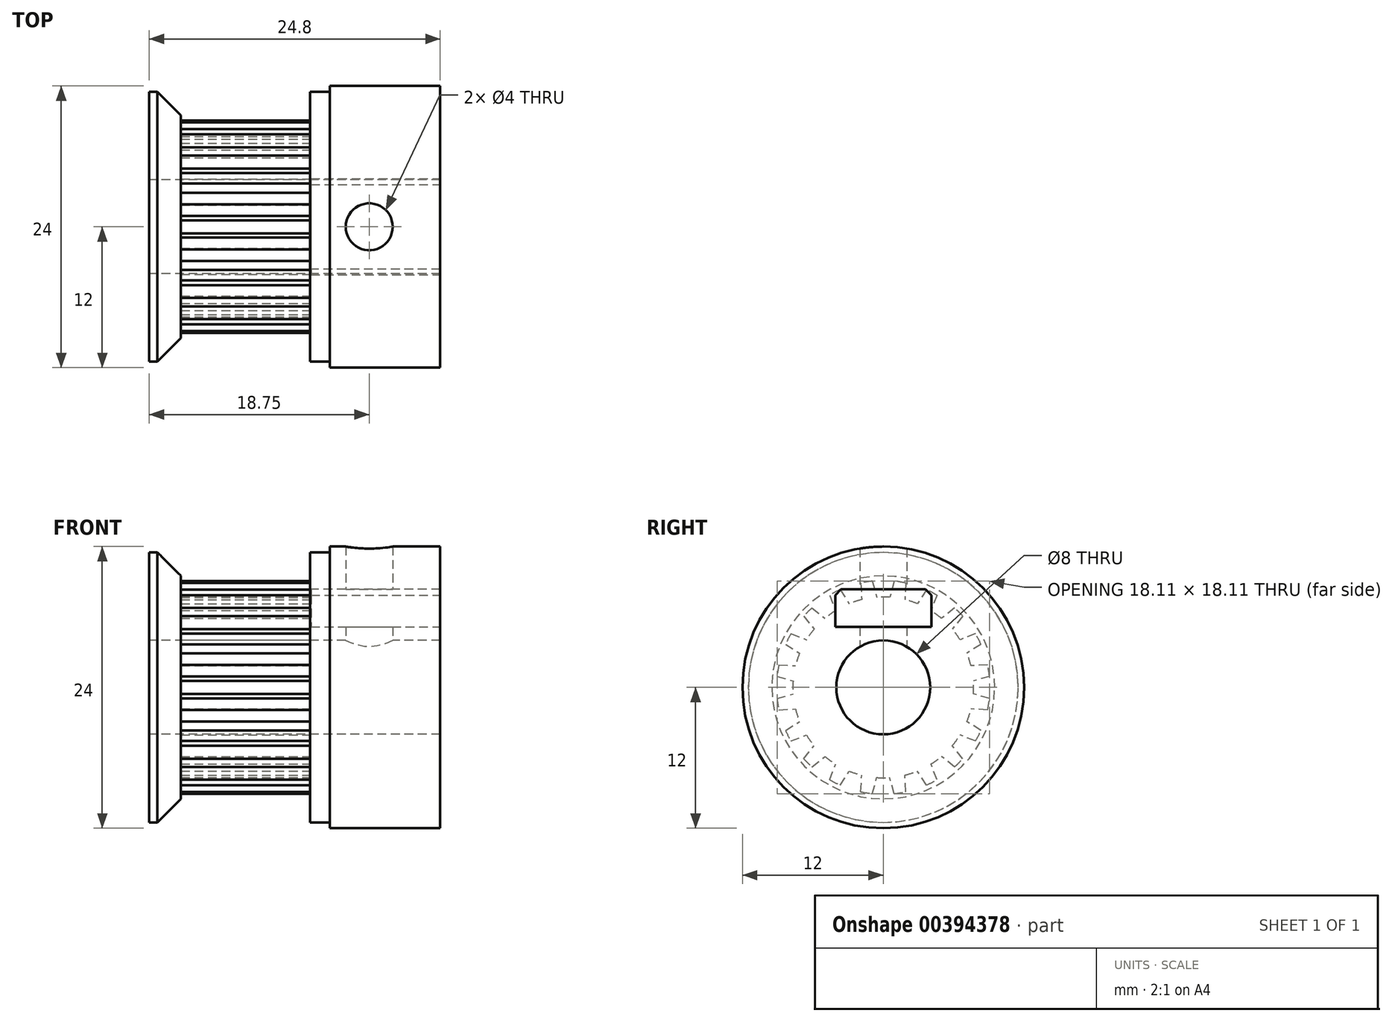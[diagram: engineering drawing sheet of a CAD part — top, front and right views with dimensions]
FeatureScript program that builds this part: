
annotation { "Feature Type Name" : "Feature", "Feature Type Description" : "" }
export const myFeature = defineFeature(function(context is Context, id is Id, definition is map)
    precondition{}
    {
        {
            var Q0;
            Q0=qCreatedBy(makeId("Top.planeOp"),FACE);
            var sketch = newSketch(context, id + "F0", { "sketchPlane" : qUnion([Q0])});
            skLineSegment(sketch, "E0", {"start": v(0, 0) * mm, "end": v(0, 231.14) * mm, "construction": true});
            skLineSegment(sketch, "E1", {"start": v(-182.88, 231.14) * mm, "end": v(182.88, 231.14) * mm});
            skPoint(sketch, "E2", {"position": v(0, 231.14) * mm});
            skLineSegment(sketch, "E3", {"start": v(-182.88, 231.14) * mm, "end": v(-182.88, 0) * mm});
            skLineSegment(sketch, "E4", {"start": v(-182.88, 101.6) * mm, "end": v(421.64, 101.6) * mm});
            skLineSegment(sketch, "E5", {"start": v(182.88, 304.8) * mm, "end": v(421.64, 304.8) * mm});
            skLineSegment(sketch, "E6", {"start": v(182.88, 304.8) * mm, "end": v(182.88, 231.14) * mm});
            skLineSegment(sketch, "E7", {"start": v(421.64, 304.8) * mm, "end": v(421.64, 101.6) * mm});
            skLineSegment(sketch, "E8", {"start": v(0, 0) * mm, "end": v(573.1, 0) * mm});
            skSolve(sketch);
        }
        {
            var Q0;
            {var subQ2=sQuery(id+"F0.wireOp",EDGE,"E1");Q0=makeQuery(id+"F0.imprint","IMPRINT",FACE,{"disambiguationData":[TD([[makeQuery(id+"F0.imprint","IMPRINT",EDGE,{"derivedFrom":subQ2}),-1.0]])]});}
            var Q1;
            Q1=sQuery(id+"F0.wireOp",EDGE,"E8");
            revolve(context, id + "F1", {"entities" : qUnion([Q0]), "axis" : qUnion([Q1]), "revolveType" : RevolveType.FULL});
        }
        {
            var Q0;
            Q0=qCreatedBy(makeId("Right.planeOp"),FACE);
            var sketch = newSketch(context, id + "F2", { "sketchPlane" : qUnion([Q0])});
            skLineSegment(sketch, "E9", {"start": v(0, 0) * mm, "end": v(0, 231.14) * mm, "construction": true});
            skLineSegment(sketch, "E10", {"start": v(23.56, 229.94) * mm, "end": v(14.22, 195.06) * mm});
            skCircle(sketch, "E11", {"center": v(0, 0) * mm, "radius": 231.14 * mm});
            skCircle(sketch, "E12", {"center": v(0, 0) * mm, "radius": 195.58 * mm});
            skLineSegment(sketch, "E13.MirrorCS", {"start": v(-23.56, 229.94) * mm, "end": v(-14.22, 195.06) * mm});
            skLineSegment(sketch, "E14.1.0", {"start": v(0, 0) * mm, "end": v(-71.43, 219.83) * mm, "construction": true});
            skLineSegment(sketch, "E14.1.1", {"start": v(-48.65, 225.96) * mm, "end": v(-46.76, 189.9) * mm});
            skLineSegment(sketch, "E14.1.2", {"start": v(-93.46, 211.4) * mm, "end": v(-73.8, 181.12) * mm});
            skLineSegment(sketch, "E14.2.0", {"start": v(0, 0) * mm, "end": v(-135.86, 187) * mm, "construction": true});
            skLineSegment(sketch, "E14.2.1", {"start": v(-116.1, 199.87) * mm, "end": v(-103.15, 166.16) * mm});
            skLineSegment(sketch, "E14.2.2", {"start": v(-154.21, 172.17) * mm, "end": v(-126.16, 149.45) * mm});
            skLineSegment(sketch, "E14.3.0", {"start": v(0, 0) * mm, "end": v(-187, 135.86) * mm, "construction": true});
            skLineSegment(sketch, "E14.3.1", {"start": v(-172.17, 154.21) * mm, "end": v(-149.45, 126.16) * mm});
            skLineSegment(sketch, "E14.3.2", {"start": v(-199.87, 116.1) * mm, "end": v(-166.16, 103.15) * mm});
            skLineSegment(sketch, "E14.4.0", {"start": v(0, 0) * mm, "end": v(-219.83, 71.43) * mm, "construction": true});
            skLineSegment(sketch, "E14.4.1", {"start": v(-211.4, 93.46) * mm, "end": v(-181.12, 73.8) * mm});
            skLineSegment(sketch, "E14.4.2", {"start": v(-225.96, 48.65) * mm, "end": v(-189.9, 46.76) * mm});
            skLineSegment(sketch, "E14.5.0", {"start": v(0, 0) * mm, "end": v(-231.14, 0) * mm, "construction": true});
            skLineSegment(sketch, "E14.5.1", {"start": v(-229.94, 23.56) * mm, "end": v(-195.06, 14.22) * mm});
            skLineSegment(sketch, "E14.5.2", {"start": v(-229.94, -23.56) * mm, "end": v(-195.06, -14.22) * mm});
            skLineSegment(sketch, "E14.6.0", {"start": v(0, 0) * mm, "end": v(-219.83, -71.43) * mm, "construction": true});
            skLineSegment(sketch, "E14.6.1", {"start": v(-225.96, -48.65) * mm, "end": v(-189.9, -46.76) * mm});
            skLineSegment(sketch, "E14.6.2", {"start": v(-211.4, -93.46) * mm, "end": v(-181.12, -73.8) * mm});
            skLineSegment(sketch, "E14.7.0", {"start": v(0, 0) * mm, "end": v(-187, -135.86) * mm, "construction": true});
            skLineSegment(sketch, "E14.7.1", {"start": v(-199.87, -116.1) * mm, "end": v(-166.16, -103.15) * mm});
            skLineSegment(sketch, "E14.7.2", {"start": v(-172.17, -154.21) * mm, "end": v(-149.45, -126.16) * mm});
            skLineSegment(sketch, "E14.8.0", {"start": v(0, 0) * mm, "end": v(-135.86, -187) * mm, "construction": true});
            skLineSegment(sketch, "E14.8.1", {"start": v(-154.21, -172.17) * mm, "end": v(-126.16, -149.45) * mm});
            skLineSegment(sketch, "E14.8.2", {"start": v(-116.1, -199.87) * mm, "end": v(-103.15, -166.16) * mm});
            skLineSegment(sketch, "E14.9.0", {"start": v(0, 0) * mm, "end": v(-71.43, -219.83) * mm, "construction": true});
            skLineSegment(sketch, "E14.9.1", {"start": v(-93.46, -211.4) * mm, "end": v(-73.8, -181.12) * mm});
            skLineSegment(sketch, "E14.9.2", {"start": v(-48.65, -225.96) * mm, "end": v(-46.76, -189.9) * mm});
            skLineSegment(sketch, "E14.10.0", {"start": v(0, 0) * mm, "end": v(0, -231.14) * mm, "construction": true});
            skLineSegment(sketch, "E14.10.1", {"start": v(-23.56, -229.94) * mm, "end": v(-14.22, -195.06) * mm});
            skLineSegment(sketch, "E14.10.2", {"start": v(23.56, -229.94) * mm, "end": v(14.22, -195.06) * mm});
            skLineSegment(sketch, "E14.11.0", {"start": v(0, 0) * mm, "end": v(71.43, -219.83) * mm, "construction": true});
            skLineSegment(sketch, "E14.11.1", {"start": v(48.65, -225.96) * mm, "end": v(46.76, -189.9) * mm});
            skLineSegment(sketch, "E14.11.2", {"start": v(93.46, -211.4) * mm, "end": v(73.8, -181.12) * mm});
            skLineSegment(sketch, "E14.12.0", {"start": v(0, 0) * mm, "end": v(135.86, -187) * mm, "construction": true});
            skLineSegment(sketch, "E14.12.1", {"start": v(116.1, -199.87) * mm, "end": v(103.15, -166.16) * mm});
            skLineSegment(sketch, "E14.12.2", {"start": v(154.21, -172.17) * mm, "end": v(126.16, -149.45) * mm});
            skLineSegment(sketch, "E14.13.0", {"start": v(0, 0) * mm, "end": v(187, -135.86) * mm, "construction": true});
            skLineSegment(sketch, "E14.13.1", {"start": v(172.17, -154.21) * mm, "end": v(149.45, -126.16) * mm});
            skLineSegment(sketch, "E14.13.2", {"start": v(199.87, -116.1) * mm, "end": v(166.16, -103.15) * mm});
            skLineSegment(sketch, "E14.14.0", {"start": v(0, 0) * mm, "end": v(219.83, -71.43) * mm, "construction": true});
            skLineSegment(sketch, "E14.14.1", {"start": v(211.4, -93.46) * mm, "end": v(181.12, -73.8) * mm});
            skLineSegment(sketch, "E14.14.2", {"start": v(225.96, -48.65) * mm, "end": v(189.9, -46.76) * mm});
            skLineSegment(sketch, "E14.15.0", {"start": v(0, 0) * mm, "end": v(231.14, 0) * mm, "construction": true});
            skLineSegment(sketch, "E14.15.1", {"start": v(229.94, -23.56) * mm, "end": v(195.06, -14.22) * mm});
            skLineSegment(sketch, "E14.15.2", {"start": v(229.94, 23.56) * mm, "end": v(195.06, 14.22) * mm});
            skLineSegment(sketch, "E14.16.0", {"start": v(0, 0) * mm, "end": v(219.83, 71.43) * mm, "construction": true});
            skLineSegment(sketch, "E14.16.1", {"start": v(225.96, 48.65) * mm, "end": v(189.9, 46.76) * mm});
            skLineSegment(sketch, "E14.16.2", {"start": v(211.4, 93.46) * mm, "end": v(181.12, 73.8) * mm});
            skLineSegment(sketch, "E14.17.0", {"start": v(0, 0) * mm, "end": v(187, 135.86) * mm, "construction": true});
            skLineSegment(sketch, "E14.17.1", {"start": v(199.87, 116.1) * mm, "end": v(166.16, 103.15) * mm});
            skLineSegment(sketch, "E14.17.2", {"start": v(172.17, 154.21) * mm, "end": v(149.45, 126.16) * mm});
            skLineSegment(sketch, "E14.18.0", {"start": v(0, 0) * mm, "end": v(135.86, 187) * mm, "construction": true});
            skLineSegment(sketch, "E14.18.1", {"start": v(154.21, 172.17) * mm, "end": v(126.16, 149.45) * mm});
            skLineSegment(sketch, "E14.18.2", {"start": v(116.1, 199.87) * mm, "end": v(103.15, 166.16) * mm});
            skLineSegment(sketch, "E14.19.0", {"start": v(0, 0) * mm, "end": v(71.43, 219.83) * mm, "construction": true});
            skLineSegment(sketch, "E14.19.1", {"start": v(93.46, 211.4) * mm, "end": v(73.8, 181.12) * mm});
            skLineSegment(sketch, "E14.19.2", {"start": v(48.65, 225.96) * mm, "end": v(46.76, 189.9) * mm});
            skSolve(sketch);
        }
        {
            var Q0;
            {var subQ0=sQuery(id+"F2.wireOp",EDGE,"E14.1.1");Q0=makeQuery(id+"F2.imprint","IMPRINT",FACE,{"disambiguationData":[TD([[makeQuery(id+"F2.imprint","IMPRINT",EDGE,{"derivedFrom":subQ0}),-1.0]])]});}
            var Q1;
            {var subQ0=sQuery(id+"F2.wireOp",EDGE,"E10");Q1=makeQuery(id+"F2.imprint","IMPRINT",FACE,{"disambiguationData":[TD([[makeQuery(id+"F2.imprint","IMPRINT",EDGE,{"derivedFrom":subQ0}),-1.0]])]});}
            var Q2;
            {var subQ0=sQuery(id+"F2.wireOp",EDGE,"E14.19.1");Q2=makeQuery(id+"F2.imprint","IMPRINT",FACE,{"disambiguationData":[TD([[makeQuery(id+"F2.imprint","IMPRINT",EDGE,{"derivedFrom":subQ0}),-1.0]])]});}
            var Q3;
            {var subQ0=sQuery(id+"F2.wireOp",EDGE,"E14.18.1");Q3=makeQuery(id+"F2.imprint","IMPRINT",FACE,{"disambiguationData":[TD([[makeQuery(id+"F2.imprint","IMPRINT",EDGE,{"derivedFrom":subQ0}),-1.0]])]});}
            var Q4;
            {var subQ0=sQuery(id+"F2.wireOp",EDGE,"E14.17.1");Q4=makeQuery(id+"F2.imprint","IMPRINT",FACE,{"disambiguationData":[TD([[makeQuery(id+"F2.imprint","IMPRINT",EDGE,{"derivedFrom":subQ0}),-1.0]])]});}
            var Q5;
            {var subQ0=sQuery(id+"F2.wireOp",EDGE,"E14.16.1");Q5=makeQuery(id+"F2.imprint","IMPRINT",FACE,{"disambiguationData":[TD([[makeQuery(id+"F2.imprint","IMPRINT",EDGE,{"derivedFrom":subQ0}),-1.0]])]});}
            var Q6;
            {var subQ0=sQuery(id+"F2.wireOp",EDGE,"E14.15.1");Q6=makeQuery(id+"F2.imprint","IMPRINT",FACE,{"disambiguationData":[TD([[makeQuery(id+"F2.imprint","IMPRINT",EDGE,{"derivedFrom":subQ0}),-1.0]])]});}
            var Q7;
            {var subQ0=sQuery(id+"F2.wireOp",EDGE,"E14.14.1");Q7=makeQuery(id+"F2.imprint","IMPRINT",FACE,{"disambiguationData":[TD([[makeQuery(id+"F2.imprint","IMPRINT",EDGE,{"derivedFrom":subQ0}),-1.0]])]});}
            var Q8;
            {var subQ0=sQuery(id+"F2.wireOp",EDGE,"E14.13.1");Q8=makeQuery(id+"F2.imprint","IMPRINT",FACE,{"disambiguationData":[TD([[makeQuery(id+"F2.imprint","IMPRINT",EDGE,{"derivedFrom":subQ0}),-1.0]])]});}
            var Q9;
            {var subQ0=sQuery(id+"F2.wireOp",EDGE,"E14.12.1");Q9=makeQuery(id+"F2.imprint","IMPRINT",FACE,{"disambiguationData":[TD([[makeQuery(id+"F2.imprint","IMPRINT",EDGE,{"derivedFrom":subQ0}),-1.0]])]});}
            var Q10;
            {var subQ0=sQuery(id+"F2.wireOp",EDGE,"E14.11.1");Q10=makeQuery(id+"F2.imprint","IMPRINT",FACE,{"disambiguationData":[TD([[makeQuery(id+"F2.imprint","IMPRINT",EDGE,{"derivedFrom":subQ0}),-1.0]])]});}
            var Q11;
            {var subQ0=sQuery(id+"F2.wireOp",EDGE,"E14.10.1");Q11=makeQuery(id+"F2.imprint","IMPRINT",FACE,{"disambiguationData":[TD([[makeQuery(id+"F2.imprint","IMPRINT",EDGE,{"derivedFrom":subQ0}),-1.0]])]});}
            var Q12;
            {var subQ0=sQuery(id+"F2.wireOp",EDGE,"E14.9.1");Q12=makeQuery(id+"F2.imprint","IMPRINT",FACE,{"disambiguationData":[TD([[makeQuery(id+"F2.imprint","IMPRINT",EDGE,{"derivedFrom":subQ0}),-1.0]])]});}
            var Q13;
            {var subQ0=sQuery(id+"F2.wireOp",EDGE,"E14.8.1");Q13=makeQuery(id+"F2.imprint","IMPRINT",FACE,{"disambiguationData":[TD([[makeQuery(id+"F2.imprint","IMPRINT",EDGE,{"derivedFrom":subQ0}),-1.0]])]});}
            var Q14;
            {var subQ0=sQuery(id+"F2.wireOp",EDGE,"E14.7.1");Q14=makeQuery(id+"F2.imprint","IMPRINT",FACE,{"disambiguationData":[TD([[makeQuery(id+"F2.imprint","IMPRINT",EDGE,{"derivedFrom":subQ0}),-1.0]])]});}
            var Q15;
            {var subQ0=sQuery(id+"F2.wireOp",EDGE,"E14.6.1");Q15=makeQuery(id+"F2.imprint","IMPRINT",FACE,{"disambiguationData":[TD([[makeQuery(id+"F2.imprint","IMPRINT",EDGE,{"derivedFrom":subQ0}),-1.0]])]});}
            var Q16;
            {var subQ0=sQuery(id+"F2.wireOp",EDGE,"E14.5.1");Q16=makeQuery(id+"F2.imprint","IMPRINT",FACE,{"disambiguationData":[TD([[makeQuery(id+"F2.imprint","IMPRINT",EDGE,{"derivedFrom":subQ0}),-1.0]])]});}
            var Q17;
            {var subQ0=sQuery(id+"F2.wireOp",EDGE,"E14.4.1");Q17=makeQuery(id+"F2.imprint","IMPRINT",FACE,{"disambiguationData":[TD([[makeQuery(id+"F2.imprint","IMPRINT",EDGE,{"derivedFrom":subQ0}),-1.0]])]});}
            var Q18;
            {var subQ0=sQuery(id+"F2.wireOp",EDGE,"E14.3.1");Q18=makeQuery(id+"F2.imprint","IMPRINT",FACE,{"disambiguationData":[TD([[makeQuery(id+"F2.imprint","IMPRINT",EDGE,{"derivedFrom":subQ0}),-1.0]])]});}
            var Q19;
            {var subQ0=sQuery(id+"F2.wireOp",EDGE,"E14.2.1");Q19=makeQuery(id+"F2.imprint","IMPRINT",FACE,{"disambiguationData":[TD([[makeQuery(id+"F2.imprint","IMPRINT",EDGE,{"derivedFrom":subQ0}),-1.0]])]});}
            var Q20;
            Q20=makeQuery(id+"F1.opRevolve","SWEPT_FACE",FACE,{"disambiguationData":[OSD([sQuery(id+"F0.wireOp",EDGE,"E6")])]});
            extrude(context, id + "F3", {"entities" : qUnion([Q0, Q1, Q2, Q3, Q4, Q5, Q6, Q7, Q8, Q9, Q10, Q11, Q12, Q13, Q14, Q15, Q16, Q17, Q18, Q19]), "operationType" : NewBodyOperationType.REMOVE, "endBound" : BoundingType.UP_TO_NEXT, "oppositeDirection" : true, "depth" : 25.4 * mm, "hasSecondDirection" : true, "secondDirectionBound" : SecondDirectionBoundingType.UP_TO_SURFACE, "secondDirectionOppositeDirection" : false, "secondDirectionBoundEntityFace" : qUnion([Q20]), "secondDirectionDepth" : 25.4 * mm});
        }
        {
            var Q0;
            Q0=qCreatedBy(makeId("Top.planeOp"),FACE);
            var sketch = newSketch(context, id + "F4", { "sketchPlane" : qUnion([Q0])});
            skLineSegment(sketch, "E15", {"start": v(-182.88, 292.1) * mm, "end": v(-182.88, -292.1) * mm});
            skPoint(sketch, "E16", {"position": v(-182.88, 0) * mm});
            skLineSegment(sketch, "E17.0", {"start": v(-182.88, 14.22) * mm, "end": v(-182.88, -14.22) * mm});
            skLineSegment(sketch, "E18", {"start": v(0, 0) * mm, "end": v(0, -406.4) * mm, "construction": true});
            skLineSegment(sketch, "E19", {"start": v(-182.88, -292.1) * mm, "end": v(-139.7, -292.1) * mm});
            skLineSegment(sketch, "E20", {"start": v(-139.7, -292.1) * mm, "end": v(-139.7, 0) * mm});
            skLineSegment(sketch, "E21", {"start": v(-139.7, 0) * mm, "end": v(-182.88, 0) * mm});
            skLineSegment(sketch, "E22.MirrorCS", {"start": v(139.7, -292.1) * mm, "end": v(139.7, 0) * mm});
            skLineSegment(sketch, "E23.MirrorCS", {"start": v(182.88, -292.1) * mm, "end": v(139.7, -292.1) * mm});
            skLineSegment(sketch, "E24.MirrorCS", {"start": v(182.88, 292.1) * mm, "end": v(182.88, -292.1) * mm});
            skLineSegment(sketch, "E25.MirrorCS", {"start": v(139.7, 0) * mm, "end": v(182.88, 0) * mm});
            skLineSegment(sketch, "E26.bottom", {"start": v(139.7, -292.1) * mm, "end": v(182.88, -292.1) * mm});
            skLineSegment(sketch, "E26.top", {"start": v(139.7, -304.8) * mm, "end": v(182.88, -304.8) * mm});
            skLineSegment(sketch, "E26.left", {"start": v(139.7, -292.1) * mm, "end": v(139.7, -304.8) * mm});
            skLineSegment(sketch, "E26.right", {"start": v(182.88, -292.1) * mm, "end": v(182.88, -304.8) * mm});
            skLineSegment(sketch, "E27", {"start": v(447.04, -304.8) * mm, "end": v(182.88, -304.8) * mm});
            skSolve(sketch);
        }
        {
            var Q0;
            {var subQ0=sQuery(id+"F4.wireOp",EDGE,"E19");Q0=makeQuery(id+"F4.imprint","IMPRINT",FACE,{"disambiguationData":[TD([[makeQuery(id+"F4.imprint","IMPRINT",EDGE,{"derivedFrom":subQ0}),1.0]])]});}
            var Q1;
            Q1=makeQuery(id+"F4.imprint","IMPRINT",FACE,{"disambiguationData":[TD([[makeQuery(id+"F4.imprint","IMPRINT",EDGE,{"derivedFrom":sQuery(id+"F4.wireOp",EDGE,"E22.MirrorCS")}),-1.0]])]});
            var Q2;
            Q2=makeQuery(id+"F4.imprint","IMPRINT",FACE,{"disambiguationData":[TD([[makeQuery(id+"F4.imprint","IMPRINT",EDGE,{"derivedFrom":sQuery(id+"F4.wireOp",EDGE,"E26.bottom")}),-1.0]])]});
            var Q3;
            Q3=sQuery(id+"F4.wireOp",EDGE,"E21");
            revolve(context, id + "F5", {"operationType" : NewBodyOperationType.ADD, "entities" : qUnion([Q0, Q1, Q2]), "axis" : qUnion([Q3]), "revolveType" : RevolveType.FULL});
        }
        {
            var Q0;
            Q0=makeQuery(id+"F5.boolean.opBoolean","SPLIT",FACE,{"derivedFrom":makeQuery(id+"F5.opRevolve","SWEPT_FACE",FACE,{"disambiguationData":[OSD([sQuery(id+"F4.wireOp",EDGE,"E24.MirrorCS")])]})});
            extrude(context, id + "F6", {"entities" : qUnion([Q0]), "operationType" : NewBodyOperationType.REMOVE, "endBound" : BoundingType.THROUGH_ALL, "oppositeDirection" : true, "depth" : 25.4 * mm});
        }
        {
            var Q0;
            Q0=makeQuery(id+"F1.opRevolve","SWEPT_FACE",FACE,{"disambiguationData":[OSD([sQuery(id+"F0.wireOp",EDGE,"E7")])]});
            var sketch = newSketch(context, id + "F7", { "sketchPlane" : qUnion([Q0])});
            skCircle(sketch, "E28.0", {"center": v(0, 0) * mm, "radius": 304.8 * mm});
            skCircle(sketch, "E29.0", {"center": v(0, 0) * mm, "radius": 101.6 * mm});
            skLineSegment(sketch, "E30.bottom", {"start": v(-104.14, 212.1) * mm, "end": v(104.14, 212.1) * mm});
            skLineSegment(sketch, "E30.top", {"start": v(-104.14, 130.81) * mm, "end": v(104.14, 130.81) * mm});
            skLineSegment(sketch, "E30.left", {"start": v(-104.14, 212.1) * mm, "end": v(-104.14, 130.81) * mm});
            skLineSegment(sketch, "E30.right", {"start": v(104.14, 212.1) * mm, "end": v(104.14, 130.81) * mm});
            skLineSegment(sketch, "E31", {"start": v(0, 304.8) * mm, "end": v(0, 101.6) * mm, "construction": true});
            skPoint(sketch, "E32", {"position": v(0, 171.45) * mm});
            skPoint(sketch, "E33", {"position": v(0, 212.1) * mm});
            skPoint(sketch, "E34", {"position": v(104.14, 171.45) * mm});
            skSolve(sketch);
        }
        {
            var Q0;
            Q0=qCreatedBy(makeId("Top.planeOp"),FACE);
            var sketch = newSketch(context, id + "F8", { "sketchPlane" : qUnion([Q0])});
            skLineSegment(sketch, "E35.0", {"start": v(114.3, 279.4) * mm, "end": v(114.3, -279.4) * mm});
            skLineSegment(sketch, "E36.0", {"start": v(421.64, 304.8) * mm, "end": v(421.64, -304.8) * mm});
            skCircle(sketch, "E37", {"center": v(267.97, 0) * mm, "radius": 50.8 * mm});
            skLineSegment(sketch, "E38", {"start": v(114.3, 0) * mm, "end": v(421.64, 0) * mm, "construction": true});
            skLineSegment(sketch, "E39", {"start": v(166.37, 0) * mm, "end": v(369.57, 0) * mm});
            skSolve(sketch);
        }
        {
            var Q0;
            Q0 = qSketchRegion(id + "F8", true);
            extrude(context, id + "F9", {"entities" : qUnion([Q0]), "operationType" : NewBodyOperationType.REMOVE, "endBound" : BoundingType.THROUGH_ALL, "depth" : 25.4 * mm});
        }
        {
            var Q0;
            Q0=makeQuery(id+"F7.imprint","IMPRINT",FACE,{"disambiguationData":[TD([[makeQuery(id+"F7.imprint","IMPRINT",EDGE,{"derivedFrom":sQuery(id+"F7.wireOp",EDGE,"E30.bottom")}),-1.0]])]});
            extrude(context, id + "F10", {"entities" : qUnion([Q0]), "operationType" : NewBodyOperationType.REMOVE, "oppositeDirection" : true, "depth" : 279.4 * mm});
        }
        {
            var Q0;
            Q0=makeQuery(id+"F10.boolean.opBoolean","COPY",EDGE,{"derivedFrom":makeQuery(id+"F10.opExtrude","SWEPT_EDGE",EDGE,{"disambiguationData":[OSD([sQuery(id+"F7.wireOp",EDGE,"E30.bottom"),sQuery(id+"F7.wireOp",EDGE,"E30.left")])]})});
            var Q1;
            Q1=makeQuery(id+"F10.boolean.opBoolean","COPY",EDGE,{"derivedFrom":makeQuery(id+"F10.opExtrude","SWEPT_EDGE",EDGE,{"disambiguationData":[OSD([sQuery(id+"F7.wireOp",EDGE,"E30.bottom"),sQuery(id+"F7.wireOp",EDGE,"E30.right")])]})});
            chamfer(context, id + "F11", {"entities" : qUnion([Q0, Q1]), "width" : 12.7 * mm, "tangentPropagation" : true});
        }
        {
            var Q0;
            Q0=makeQuery(id+"F1.opRevolve","SWEPT_BODY",BODY,{"disambiguationData":[OSD([sQuery(id+"F0.wireOp",EDGE,"E1"),sQuery(id+"F0.wireOp",EDGE,"E3"),sQuery(id+"F0.wireOp",EDGE,"E4"),sQuery(id+"F0.wireOp",EDGE,"E5"),sQuery(id+"F0.wireOp",EDGE,"E6"),sQuery(id+"F0.wireOp",EDGE,"E7")])]});
            var Q1;
            Q1=qCreatedBy(makeId("Origin.pointOp"),VERTEX);
            transform(context, id + "F12", {"entities" : qUnion([Q0]), "transformType" : TransformType.SCALE_UNIFORMLY, "scale" : 1 / 25.4, "scalePoint" : qUnion([Q1]), "makeCopy" : false});
        }
        {
            var Q0;
            Q0=makeQuery(id+"F5.boolean.opBoolean","MERGE",FACE,{"derivedFrom":[makeQuery(id+"F1.opRevolve","SWEPT_FACE",FACE,{"disambiguationData":[OSD([sQuery(id+"F0.wireOp",EDGE,"E3")])]}),makeQuery(id+"F5.opRevolve","SWEPT_FACE",FACE,{"disambiguationData":[OSD([sQuery(id+"F4.wireOp",EDGE,"E15"),sQuery(id+"F4.wireOp",EDGE,"E17.0")])]})]});
            extrude(context, id + "F13", {"entities" : qUnion([Q0]), "operationType" : NewBodyOperationType.ADD, "depth" : 1 * mm});
        }
        {
            var Q0;
            Q0=makeQuery(id+"F5.opRevolve","SWEPT_EDGE",EDGE,{"disambiguationData":[OSD([sQuery(id+"F4.wireOp",EDGE,"E19"),sQuery(id+"F4.wireOp",EDGE,"E20")])]});
            chamfer(context, id + "F14", {"entities" : qUnion([Q0]), "width" : 2 * mm, "tangentPropagation" : true});
        }
    });
